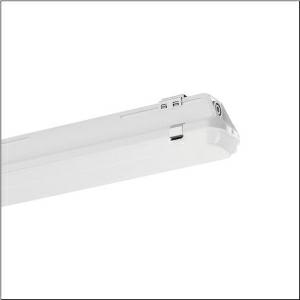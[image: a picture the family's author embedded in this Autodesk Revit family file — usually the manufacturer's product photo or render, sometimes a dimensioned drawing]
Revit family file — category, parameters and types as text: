
# Revit family: monsun_r__12_51fp207p4b0q_a0aa
name_source: partatom
category: Lighting Fixtures
units: mm (PartAtom-declared; Revit-internal decimal feet)

## family parameters
Cut with Voids When Loaded = No
Host = Face
Light Source = No
Part Type = Normal
Room Calculation Point = No
Round Connector Dimension = Use Diameter
Shared = No

## types (1)
- Monsun® 12 (1 x LED, 10910 lm, 66.2 W, 4000K)
    Apparent Load = 66 VA
    CIE Flux Codes = 45 75 93 94 100
    Color Rendering = 80
    Color Temperature = 4000K
    Default Elevation = 1800 mm
    Description = Monsun® 12, damp-proof luminaire, chain hanger, primary optical cover: enclosure, of PC, light emission: direct distribution, primary light characteristic: symmetric, installation type: suspended mounting, surface-mounted, horizontal mounting, vertical mounting, LED rated luminous flux: 10.910 lm, light colour: 840, colour temperature: 4000K, control gear: ECG, with terminal, 3-pole, max. 2.5mm², mains connection: 220..240V, AC, 50/60Hz, rated input power: 66W, luminaire housing, of glass-fibre reinforced polyester, uncoated, bright grey, length: 1.590 mm, width: 90 mm, height: 88mm, clip for enclosure, of stainless steel (V2A), ceiling mounting element, of stainless steel (V2A), chain hanger, of stainless steel (V2A), protection rating (complete): IP66, insulation class (complete): insulation class I (protective earthing), certification: CE, ENEC, VDE, protection symbol: D, impact resistance: IK08, permissible ambient temperature for indoor applications: -35..+35°C, standard: EN 50419, EN 60598-2-1, no direct snow, no direct sun, no direct rain, for indoor or canopied outdoor use, corresponds to IFS (International Featured Standards) requirements for safety and quality in the food industry, packaging unit: 1 piece
    Height = 89 mm
    Lamp = 1 x LED
    Lamp Light Flux = 10910 lm
    Lamp Power = 66.2 W
    Lamp count = 1
    Length = 1590 mm
    Luminous efficacy = 165 lm/W
    Manufacturer = Siteco
    ModVariant = No
    Model = 51FP207P4B0Q
    Mounting Place = Ceiling
    Mounting Type = Pendant
    Number of Poles = 1
    OnlyDefault = Yes
    Power Factor = 1
    Product Name = Monsun® 12
    Product group = damp-proof luminaire | ceiling pendant
    ProductGroupID = 908
    Protection Class = Protection class I
    Protection Degree = IP 66
    RLX_Detail_Level = 1
    RlxData = <blob elided: 88141 chars, md5=48fb6d95>
    Socket = socket
    Standby Power = 0 W
    System Light Flux = 10910 lm
    System Power = 66 W
    Type Comments = Product without accessories
    Type Image = l_1004748.jpg
    URL = http://relux.com
    VarID = ---
    Voltage = 0 V
    Weight = 0.00 kg
    Width = 90 mm

## geometry (parser evidence)
native form markers: Blend x4, Sweep x13
no freeform markers — native parametric forms only
